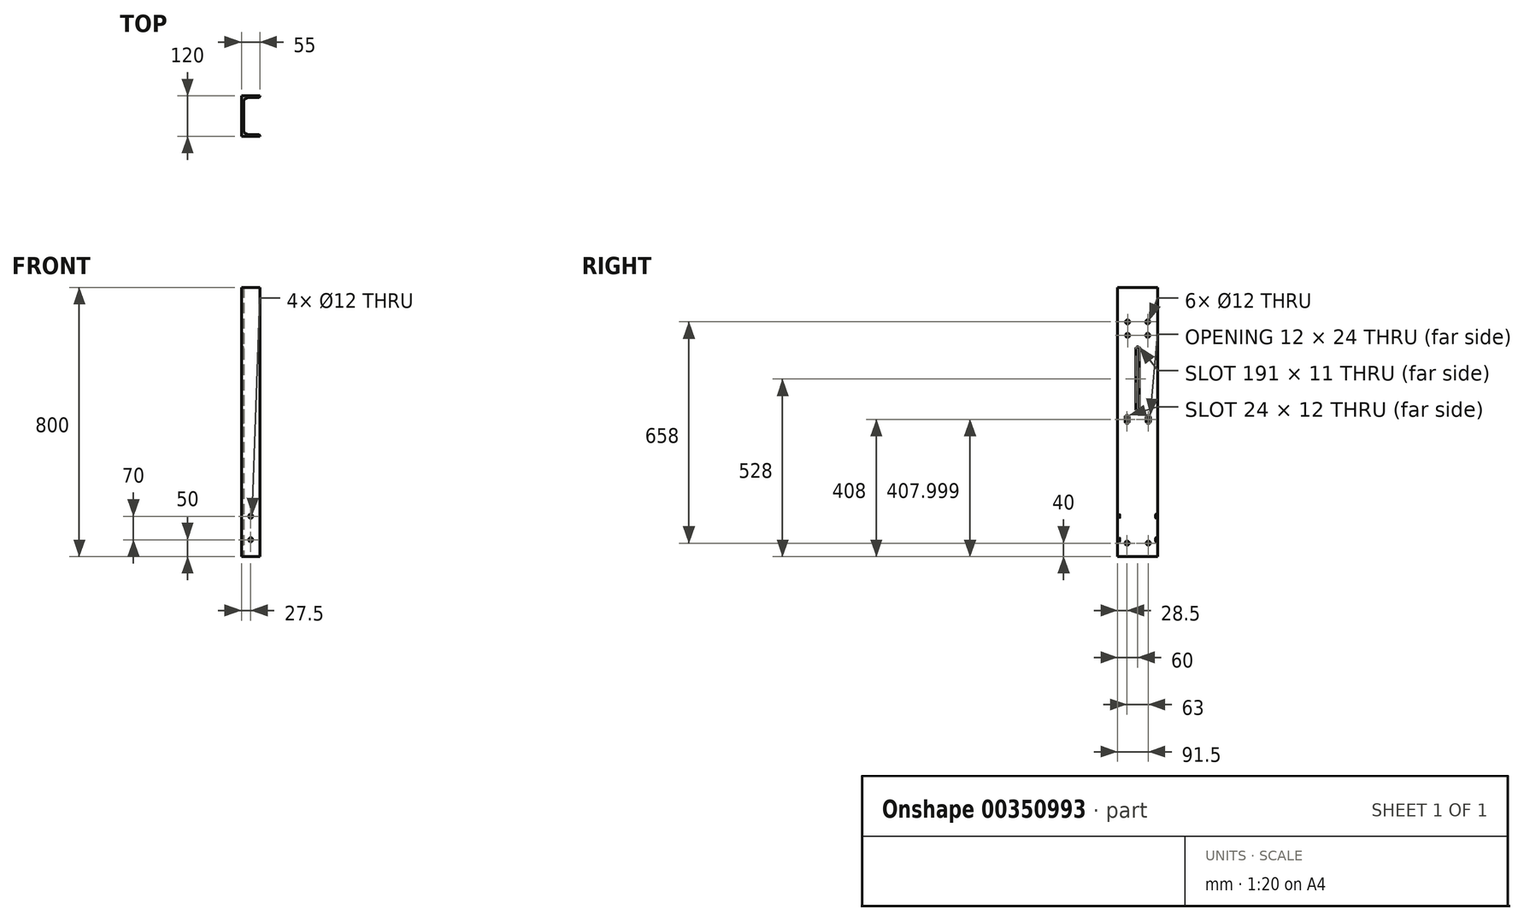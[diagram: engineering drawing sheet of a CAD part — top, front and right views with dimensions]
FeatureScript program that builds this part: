
annotation { "Feature Type Name" : "Feature", "Feature Type Description" : "" }
export const myFeature = defineFeature(function(context is Context, id is Id, definition is map)
    precondition{}
    {
        {
            var Q0;
            Q0=qCreatedBy(makeId("Top.planeOp"),FACE);
            var sketch = newSketch(context, id + "F0", { "sketchPlane" : qUnion([Q0])});
            skLineSegment(sketch, "E0", {"start": v(0, 0) * mm, "end": v(0, 120) * mm});
            skLineSegment(sketch, "E1", {"start": v(0, 120) * mm, "end": v(55, 120) * mm});
            skLineSegment(sketch, "E2", {"start": v(0, 0) * mm, "end": v(55, 0) * mm});
            skLineSegment(sketch, "E3.0", {"start": v(7, 16.6) * mm, "end": v(7, 103.4) * mm});
            skLineSegment(sketch, "E4", {"start": v(55, 0) * mm, "end": v(55, 0.68) * mm});
            skLineSegment(sketch, "E5", {"start": v(50.69, 5.18) * mm, "end": v(16.58, 6.6) * mm});
            skArc(sketch, "E6.filletArc", {"start": v(7, 16.6) * mm, "mid": v(9.78, 9.67) * mm, "end": v(16.58, 6.6) * mm});
            skPoint(sketch, "E7.visualSharp", {"position": v(55, 5) * mm});
            skArc(sketch, "E7.filletArc", {"start": v(55, 0.68) * mm, "mid": v(53.75, 3.8) * mm, "end": v(50.69, 5.18) * mm});
            skLineSegment(sketch, "E8", {"start": v(55, 120) * mm, "end": v(55, 119.32) * mm});
            skLineSegment(sketch, "E9", {"start": v(50.69, 114.82) * mm, "end": v(16.58, 113.4) * mm});
            skArc(sketch, "E10.filletArc", {"start": v(16.58, 113.4) * mm, "mid": v(9.78, 110.33) * mm, "end": v(7, 103.4) * mm});
            skPoint(sketch, "E11.visualSharp", {"position": v(55, 115) * mm});
            skArc(sketch, "E11.filletArc", {"start": v(50.69, 114.82) * mm, "mid": v(53.75, 116.2) * mm, "end": v(55, 119.32) * mm});
            skSolve(sketch);
        }
        {
            var Q0;
            Q0=makeQuery(id+"F0.imprint","IMPRINT",FACE,{"disambiguationData":[TD([[makeQuery(id+"F0.imprint","IMPRINT",EDGE,{"derivedFrom":sQuery(id+"F0.wireOp",EDGE,"E0")}),-1.0]])]});
            extrude(context, id + "F1", {"entities" : qUnion([Q0]), "endBound" : BoundingType.SYMMETRIC, "depth" : 800 * mm});
        }
        {
            var Q0;
            Q0=makeQuery(id+"F1.opExtrude","SWEPT_FACE",FACE,{"disambiguationData":[OSD([sQuery(id+"F0.wireOp",EDGE,"E0")])]});
            var sketch = newSketch(context, id + "F2", { "sketchPlane" : qUnion([Q0])});
            skLineSegment(sketch, "E12", {"start": v(-106, -360) * mm, "end": v(-0.49, -360) * mm, "construction": true});
            skLineSegment(sketch, "E13", {"start": v(-60, -400) * mm, "end": v(-60, 298) * mm, "construction": true});
            skLineSegment(sketch, "E14.0", {"start": v(-28.5, -400) * mm, "end": v(-28.5, 8) * mm, "construction": true});
            skLineSegment(sketch, "E15.0", {"start": v(-91.5, -400) * mm, "end": v(-91.5, 8) * mm, "construction": true});
            skCircle(sketch, "E16", {"center": v(-91.5, -360) * mm, "radius": 6 * mm});
            skCircle(sketch, "E17", {"center": v(-28.5, -360) * mm, "radius": 6 * mm});
            skLineSegment(sketch, "E18.0", {"start": v(-106, 8) * mm, "end": v(-0.49, 8) * mm, "construction": true});
            skLineSegment(sketch, "E19.0", {"start": v(-115, -395) * mm, "end": v(-5, -395) * mm});
            skLineSegment(sketch, "E19.1", {"start": v(-115, 395) * mm, "end": v(-115, -395) * mm});
            skLineSegment(sketch, "E19.2", {"start": v(-5, 395) * mm, "end": v(-115, 395) * mm});
            skLineSegment(sketch, "E19.3", {"start": v(-5, -395) * mm, "end": v(-5, 395) * mm});
            skArc(sketch, "E20", {"start": v(-97.5, 8.19) * mm, "mid": v(-97.5, 8) * mm, "end": v(-97.5, 7.82) * mm});
            skLineSegment(sketch, "E21.0", {"start": v(-106, 228) * mm, "end": v(-0.49, 228) * mm, "construction": true});
            skLineSegment(sketch, "E22.0", {"start": v(-106, 258) * mm, "end": v(-0.49, 258) * mm, "construction": true});
            skLineSegment(sketch, "E23.0", {"start": v(-106, 298) * mm, "end": v(-0.49, 298) * mm, "construction": true});
            skLineSegment(sketch, "E24", {"start": v(-90, 201.68) * mm, "end": v(-90, 305.23) * mm, "construction": true});
            skLineSegment(sketch, "E25", {"start": v(-30, 205.01) * mm, "end": v(-30, 305.23) * mm, "construction": true});
            skCircle(sketch, "E26", {"center": v(-90, 258) * mm, "radius": 6 * mm});
            skCircle(sketch, "E27", {"center": v(-30, 258) * mm, "radius": 6 * mm});
            skCircle(sketch, "E28", {"center": v(-90, 298) * mm, "radius": 6 * mm});
            skCircle(sketch, "E29", {"center": v(-30, 298) * mm, "radius": 6 * mm});
            skLineSegment(sketch, "E30.0", {"start": v(-106, 38) * mm, "end": v(-0.49, 38) * mm, "construction": true});
            skLineSegment(sketch, "E31.0", {"start": v(-106, 218) * mm, "end": v(-0.49, 218) * mm, "construction": true});
            skArc(sketch, "E32", {"start": v(-85.5, 14) * mm, "mid": v(-91.63, 20) * mm, "end": v(-97.5, 13.74) * mm});
            skArc(sketch, "E33", {"start": v(-22.5, 14) * mm, "mid": v(-28.5, 20) * mm, "end": v(-34.5, 14) * mm});
            skArc(sketch, "E34", {"start": v(-97.5, 2) * mm, "mid": v(-91.5, -4) * mm, "end": v(-85.5, 2) * mm});
            skArc(sketch, "E35", {"start": v(-34.5, 2) * mm, "mid": v(-28.5, -4) * mm, "end": v(-22.5, 2) * mm});
            skLineSegment(sketch, "E36", {"start": v(-97.5, 2) * mm, "end": v(-97.5, 13.74) * mm});
            skLineSegment(sketch, "E37", {"start": v(-85.5, 14) * mm, "end": v(-85.5, 2) * mm});
            skLineSegment(sketch, "E38", {"start": v(-34.5, 2) * mm, "end": v(-34.5, 14) * mm});
            skLineSegment(sketch, "E39", {"start": v(-22.5, 2) * mm, "end": v(-22.5, 14) * mm});
            skArc(sketch, "E40.0", {"start": v(-65.5, 38) * mm, "mid": v(-60, 32.5) * mm, "end": v(-54.5, 38) * mm});
            skLineSegment(sketch, "E40.1", {"start": v(-65.5, 218) * mm, "end": v(-65.5, 38) * mm});
            skArc(sketch, "E40.2", {"start": v(-54.5, 218) * mm, "mid": v(-60, 223.5) * mm, "end": v(-65.5, 218) * mm});
            skLineSegment(sketch, "E40.3", {"start": v(-54.5, 38) * mm, "end": v(-54.5, 218) * mm});
            skSolve(sketch);
        }
        {
            var Q0;
            Q0=makeQuery(id+"F2.imprint","IMPRINT",FACE,{"disambiguationData":[TD([[makeQuery(id+"F2.imprint","IMPRINT",EDGE,{"derivedFrom":sQuery(id+"F2.wireOp",EDGE,"E28")}),1.0]])]});
            var Q1;
            Q1=makeQuery(id+"F2.imprint","IMPRINT",FACE,{"disambiguationData":[TD([[makeQuery(id+"F2.imprint","IMPRINT",EDGE,{"derivedFrom":sQuery(id+"F2.wireOp",EDGE,"E29")}),1.0]])]});
            var Q2;
            Q2=makeQuery(id+"F2.imprint","IMPRINT",FACE,{"disambiguationData":[TD([[makeQuery(id+"F2.imprint","IMPRINT",EDGE,{"derivedFrom":sQuery(id+"F2.wireOp",EDGE,"E27")}),1.0]])]});
            var Q3;
            Q3=makeQuery(id+"F2.imprint","IMPRINT",FACE,{"disambiguationData":[TD([[makeQuery(id+"F2.imprint","IMPRINT",EDGE,{"derivedFrom":sQuery(id+"F2.wireOp",EDGE,"E26")}),1.0]])]});
            var Q4;
            Q4=makeQuery(id+"F2.imprint","IMPRINT",FACE,{"disambiguationData":[TD([[makeQuery(id+"F2.imprint","IMPRINT",EDGE,{"derivedFrom":sQuery(id+"F2.wireOp",EDGE,"E20")}),1.0]])]});
            var Q5;
            Q5=makeQuery(id+"F2.imprint","IMPRINT",FACE,{"disambiguationData":[TD([[makeQuery(id+"F2.imprint","IMPRINT",EDGE,{"derivedFrom":sQuery(id+"F2.wireOp",EDGE,"R6BpRdOE-wAr9-DM0o-DmmJ-2KGXCHRUu6yd")}),1.0]])]});
            var Q6;
            Q6=makeQuery(id+"F2.imprint","IMPRINT",FACE,{"disambiguationData":[TD([[makeQuery(id+"F2.imprint","IMPRINT",EDGE,{"derivedFrom":sQuery(id+"F2.wireOp",EDGE,"E16")}),1.0]])]});
            var Q7;
            Q7=makeQuery(id+"F2.imprint","IMPRINT",FACE,{"disambiguationData":[TD([[makeQuery(id+"F2.imprint","IMPRINT",EDGE,{"derivedFrom":sQuery(id+"F2.wireOp",EDGE,"E17")}),1.0]])]});
            var Q8;
            Q8=makeQuery(id+"F2.imprint","IMPRINT",FACE,{"disambiguationData":[TD([[makeQuery(id+"F2.imprint","IMPRINT",EDGE,{"derivedFrom":sQuery(id+"F2.wireOp",EDGE,"qEUA4X6m-4Z9o-gX8K-VtGT-hELA1gRtnqrU")}),1.0]])]});
            var Q9;
            {var subQ5=sQuery(id+"F2.wireOp",EDGE,"E32");Q9=makeQuery(id+"F2.imprint","IMPRINT",FACE,{"disambiguationData":[TD([[makeQuery(id+"F2.imprint","IMPRINT",EDGE,{"derivedFrom":subQ5}),1.0]])]});}
            var Q10;
            Q10=makeQuery(id+"F2.imprint","IMPRINT",FACE,{"disambiguationData":[TD([[makeQuery(id+"F2.imprint","IMPRINT",EDGE,{"derivedFrom":sQuery(id+"F2.wireOp",EDGE,"E33")}),1.0]])]});
            var Q11;
            Q11=makeQuery(id+"F2.imprint","IMPRINT",FACE,{"disambiguationData":[TD([[makeQuery(id+"F2.imprint","IMPRINT",EDGE,{"derivedFrom":sQuery(id+"F2.wireOp",EDGE,"E40.0")}),1.0]])]});
            extrude(context, id + "F3", {"entities" : qUnion([Q0, Q1, Q2, Q3, Q4, Q5, Q6, Q7, Q8, Q9, Q10, Q11]), "operationType" : NewBodyOperationType.REMOVE, "endBound" : BoundingType.THROUGH_ALL, "oppositeDirection" : true, "depth" : 25 * mm});
        }
        {
            var Q0;
            Q0=makeQuery(id+"F1.opExtrude","SWEPT_FACE",FACE,{"disambiguationData":[OSD([sQuery(id+"F0.wireOp",EDGE,"E2")])]});
            var sketch = newSketch(context, id + "F4", { "sketchPlane" : qUnion([Q0])});
            skLineSegment(sketch, "E41", {"start": v(27.5, -454.7) * mm, "end": v(27.5, -259.74) * mm, "construction": true});
            skLineSegment(sketch, "E42", {"start": v(-52.2, -350) * mm, "end": v(115.92, -350) * mm, "construction": true});
            skLineSegment(sketch, "E43", {"start": v(-61.18, -280) * mm, "end": v(113.85, -280) * mm, "construction": true});
            skCircle(sketch, "E44", {"center": v(27.5, -350) * mm, "radius": 6 * mm});
            skCircle(sketch, "E45", {"center": v(27.5, -280) * mm, "radius": 6 * mm});
            skSolve(sketch);
        }
        {
            var Q0;
            Q0=makeQuery(id+"F4.imprint","IMPRINT",FACE,{"disambiguationData":[TD([[makeQuery(id+"F4.imprint","IMPRINT",EDGE,{"derivedFrom":sQuery(id+"F4.wireOp",EDGE,"E45")}),1.0]])]});
            var Q1;
            Q1=makeQuery(id+"F4.imprint","IMPRINT",FACE,{"disambiguationData":[TD([[makeQuery(id+"F4.imprint","IMPRINT",EDGE,{"derivedFrom":sQuery(id+"F4.wireOp",EDGE,"E44")}),1.0]])]});
            extrude(context, id + "F5", {"entities" : qUnion([Q0, Q1]), "operationType" : NewBodyOperationType.REMOVE, "endBound" : BoundingType.THROUGH_ALL, "oppositeDirection" : true, "depth" : 25 * mm});
        }
    });
